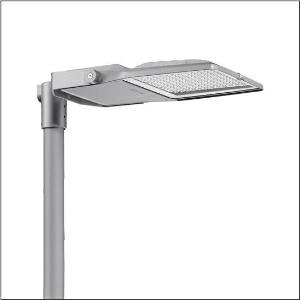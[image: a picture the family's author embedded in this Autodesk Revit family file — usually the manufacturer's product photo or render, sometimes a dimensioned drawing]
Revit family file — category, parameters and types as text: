
# Revit family: floodlight_fl_21_iq_midi___pl43_5xa7782e4a3a_f2c8
name_source: partatom
category: Lighting Fixtures
units: mm (PartAtom-declared; Revit-internal decimal feet)

## family parameters
Cut with Voids When Loaded = No
Host = Face
Light Source = No
Part Type = Normal
Room Calculation Point = No
Round Connector Dimension = Use Diameter
Shared = No

## types (1)
- --- (1 x LED, 28730 lm, 208.1 W, 4000K)
    Apparent Load = 208 VA
    CIE Flux Codes = 27 78 99 100 100
    Color Rendering = 70
    Color Temperature = 4000K
    Default Elevation = 1800 mm
    Description = Floodlight FL 21 iQ midi, floodlight, primary light control with lens, of PMMA, primary optical cover: protective disc, of toughened safety glass, transparent, light distribution: PL43, light emission: direct distribution, installation type: surface-mounted, LED, High Power LED, rated luminous flux: 28.730lm, luminous efficacy: 138lm/W, light colour: 740, colour temperature: 4000K, control gear: ECG iQ, control: optimised constant luminous flux control (CLO 2.0), Desk-Remote (wireless, voltage-free reading and setting of iQ features in the workshop via application-optimized NFC function/RFID function), Smart-Wire, Night-Set, Temp-Guard, Auto-Match, Street-Remote, with terminal, 6-pole, mains connection: 220..240V, AC, 50/60Hz, start of lifetime: 208W, end of service life: 227W, reduction: 90W, luminaire housing, of diecast aluminium, powder-coated, Siteco® metallic grey (DB 702S), corrosivity category C5 mid according to DIN EN ISO 12944, sealing non-destructively replaceable, please order mast flange separately, mast bracket, of steel, galvanised, powder-coated, Siteco® metallic grey (DB 702S), protection rating (complete): IP66, insulation class (complete): insulation class II (safety insulation), certification: CE, protection symbol: D, impact resistance: IK08, permissible operating ambient temperature: -40..+40°C, permissible operating ambient temperature for outdoor applications: -40..+50°C, standard: DIN EN 12944, LABS conformity tested according to VDMA 24364:2018-05, packaging unit: 1 piece

Light Distribution: PL43
    Height = 76 mm
    Lamp = 1 x LED
    Lamp Light Flux = 28730 lm
    Lamp Power = 208.1 W
    Lamp count = 1
    Length = 657 mm
    Luminous efficacy = 138 lm/W
    Manufacturer = Siteco
    ModVariant = No
    Model = 5XA7782E4A3A
    Number of Poles = 1
    OnlyDefault = Yes
    Power Factor = 1
    Product Name = Floodlight FL 21 iQ midi | PL43
    Product group = floodlight | pylon annexe
    ProductGroupID = 6200
    Protection Class = Protection class II
    Protection Degree = IP 66
    RLX_Detail_Level = 1
    RLX_Emergency_Light_Flux = 0 lm
    RLX_Emergency_Type = 0
    RLX_Emergency_Type_DB = No
    RlxData = <blob elided: 153485 chars, md5=b2c71aad>
    Socket = socket
    Standby Power = 0 W
    System Light Flux = 28730 lm
    System Power = 208 W
    Type Comments = factory setting: luminous flux: 100 % | dim-lin: 254 | 710 mA
    Type Image = l_1007123.jpg
    URL = http://relux.com
    VarID = @adj_035199
    Voltage = 0 V
    Weight = 0.00 kg
    Width = 442 mm

## geometry (parser evidence)
native form markers: Blend x4, Sweep x12
no freeform markers — native parametric forms only
